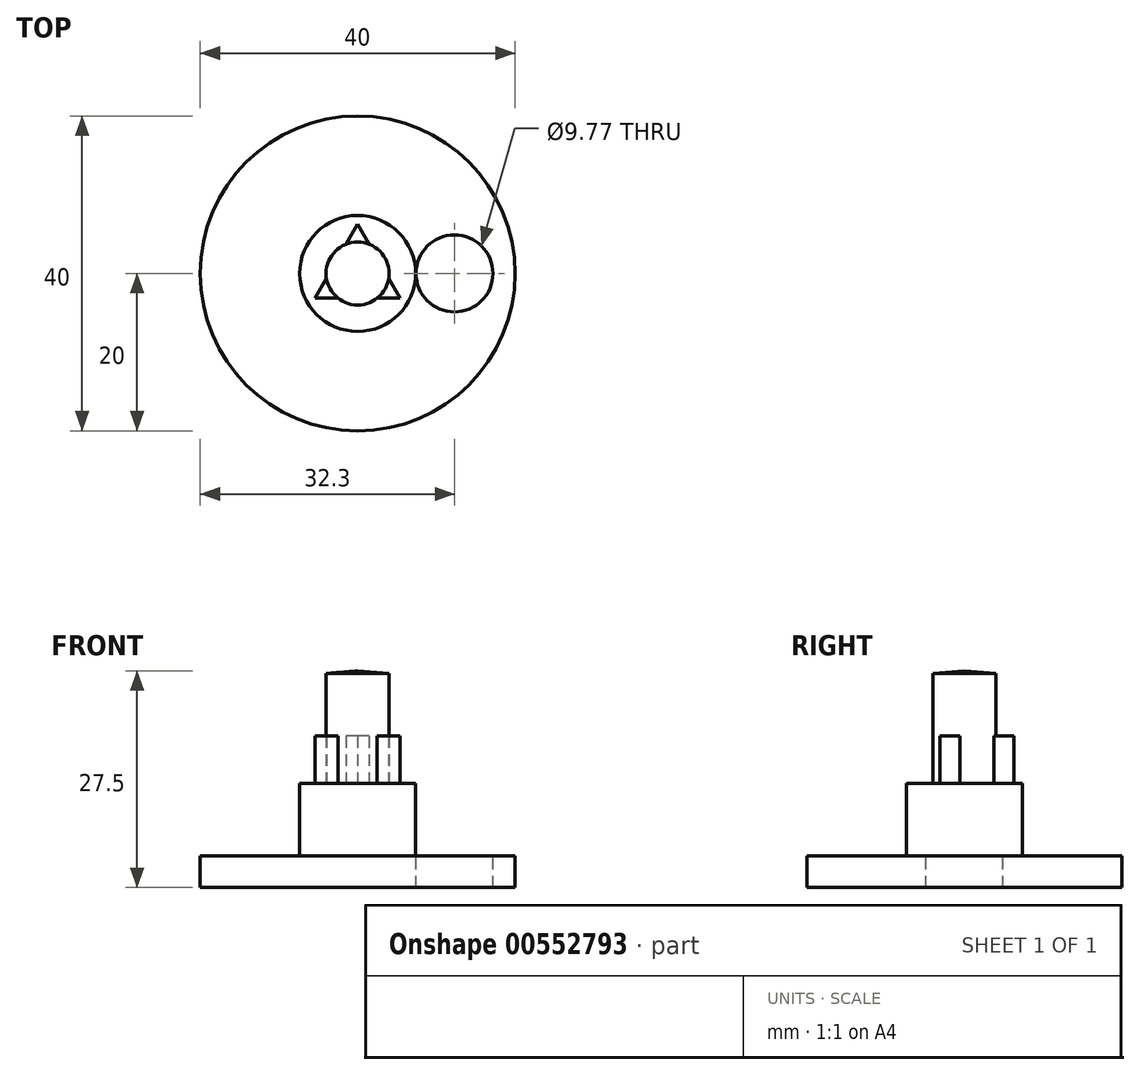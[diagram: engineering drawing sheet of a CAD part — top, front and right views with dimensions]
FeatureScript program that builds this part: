
annotation { "Feature Type Name" : "Feature", "Feature Type Description" : "" }
export const myFeature = defineFeature(function(context is Context, id is Id, definition is map)
    precondition{}
    {
        {
            var Q0;
            Q0=qCreatedBy(makeId("Front.planeOp"),FACE);
            var sketch = newSketch(context, id + "F0", { "sketchPlane" : qUnion([Q0])});
            skPoint(sketch, "E0.0", {"position": v(-5.65, 5.6) * mm});
            skLineSegment(sketch, "E1", {"start": v(-20, -9.75) * mm, "end": v(-20, -13.75) * mm});
            skLineSegment(sketch, "E2", {"start": v(-20, -13.75) * mm, "end": v(0, -13.75) * mm});
            skLineSegment(sketch, "E3", {"start": v(0, -13.75) * mm, "end": v(0, 13.75) * mm});
            skLineSegment(sketch, "E4", {"start": v(0, 13.75) * mm, "end": v(-4, 13.42) * mm});
            skLineSegment(sketch, "E5", {"start": v(-4, 13.42) * mm, "end": v(-4, -0.52) * mm});
            skLineSegment(sketch, "E6", {"start": v(-4, -0.52) * mm, "end": v(-7.37, -0.52) * mm});
            skLineSegment(sketch, "E7", {"start": v(-7.37, -0.52) * mm, "end": v(-7.37, -9.75) * mm});
            skLineSegment(sketch, "E8", {"start": v(-7.37, -9.75) * mm, "end": v(-20, -9.75) * mm});
            skSolve(sketch);
        }
        {
            var Q0;
            Q0=qSketchRegion(id+"F0",true);
            var Q1;
            Q1=sQuery(id+"F0.wireOp",EDGE,"E3");
            revolve(context, id + "F1", {"entities" : qUnion([Q0]), "axis" : qUnion([Q1]), "revolveType" : RevolveType.FULL});
        }
        {
            var Q0;
            Q0=makeQuery(id+"F1.opRevolve","SWEPT_FACE",FACE,{"disambiguationData":[OSD([sQuery(id+"F0.wireOp",EDGE,"E6")])]});
            var sketch = newSketch(context, id + "F2", { "sketchPlane" : qUnion([Q0])});
            skLineSegment(sketch, "E9", {"start": v(1.46, 3.72) * mm, "end": v(0, 6.25) * mm});
            skLineSegment(sketch, "E10", {"start": v(0, 6.25) * mm, "end": v(-1.46, 3.72) * mm});
            skLineSegment(sketch, "E11", {"start": v(-1.46, 3.72) * mm, "end": v(1.46, 3.72) * mm});
            skCircle(sketch, "E12", {"center": v(0, 0) * mm, "radius": 6.25 * mm, "construction": true});
            skCircle(sketch, "E13.0", {"center": v(0, 0) * mm, "radius": 4 * mm, "construction": true});
            skLineSegment(sketch, "E14.1.0", {"start": v(-5.41, -3.12) * mm, "end": v(-2.5, -3.12) * mm});
            skLineSegment(sketch, "E14.1.1", {"start": v(-3.95, -0.6) * mm, "end": v(-5.41, -3.12) * mm});
            skLineSegment(sketch, "E14.1.2", {"start": v(-2.5, -3.12) * mm, "end": v(-3.95, -0.6) * mm});
            skLineSegment(sketch, "E14.2.0", {"start": v(5.41, -3.12) * mm, "end": v(3.95, -0.6) * mm});
            skLineSegment(sketch, "E14.2.1", {"start": v(2.5, -3.12) * mm, "end": v(5.41, -3.12) * mm});
            skLineSegment(sketch, "E14.2.2", {"start": v(3.95, -0.6) * mm, "end": v(2.5, -3.12) * mm});
            skSolve(sketch);
        }
        {
            var Q0;
            Q0=qSketchRegion(id+"F2",true);
            extrude(context, id + "F3", {"entities" : qUnion([Q0]), "operationType" : NewBodyOperationType.ADD, "depth" : 6 * mm, "offsetDistance" : 25 * mm});
        }
        {
            var Q0;
            Q0=makeQuery(id+"F1.opRevolve","SWEPT_FACE",FACE,{"disambiguationData":[OSD([sQuery(id+"F0.wireOp",EDGE,"E8")])]});
            var sketch = newSketch(context, id + "F4", { "sketchPlane" : qUnion([Q0])});
            skCircle(sketch, "E15", {"center": v(12.3, 0) * mm, "radius": 4.89 * mm});
            skSolve(sketch);
        }
        {
            var Q0;
            Q0=makeQuery(id+"F4.imprint","IMPRINT",FACE,{"disambiguationData":[TD([[makeQuery(id+"F4.imprint","IMPRINT",EDGE,{"derivedFrom":sQuery(id+"F4.wireOp",EDGE,"E15")}),1.0]])]});
            var Q1;
            Q1=qConstructionFilter(qBodyType(qCreatedBy(id+"F4",EDGE),BodyType.WIRE),ConstructionObject.NO);
            extrude(context, id + "F5", {"entities" : qUnion([Q0]), "operationType" : NewBodyOperationType.REMOVE, "surfaceEntities" : qUnion([Q1]), "endBound" : BoundingType.THROUGH_ALL, "oppositeDirection" : true, "depth" : 25 * mm, "offsetDistance" : 25 * mm});
        }
    });
